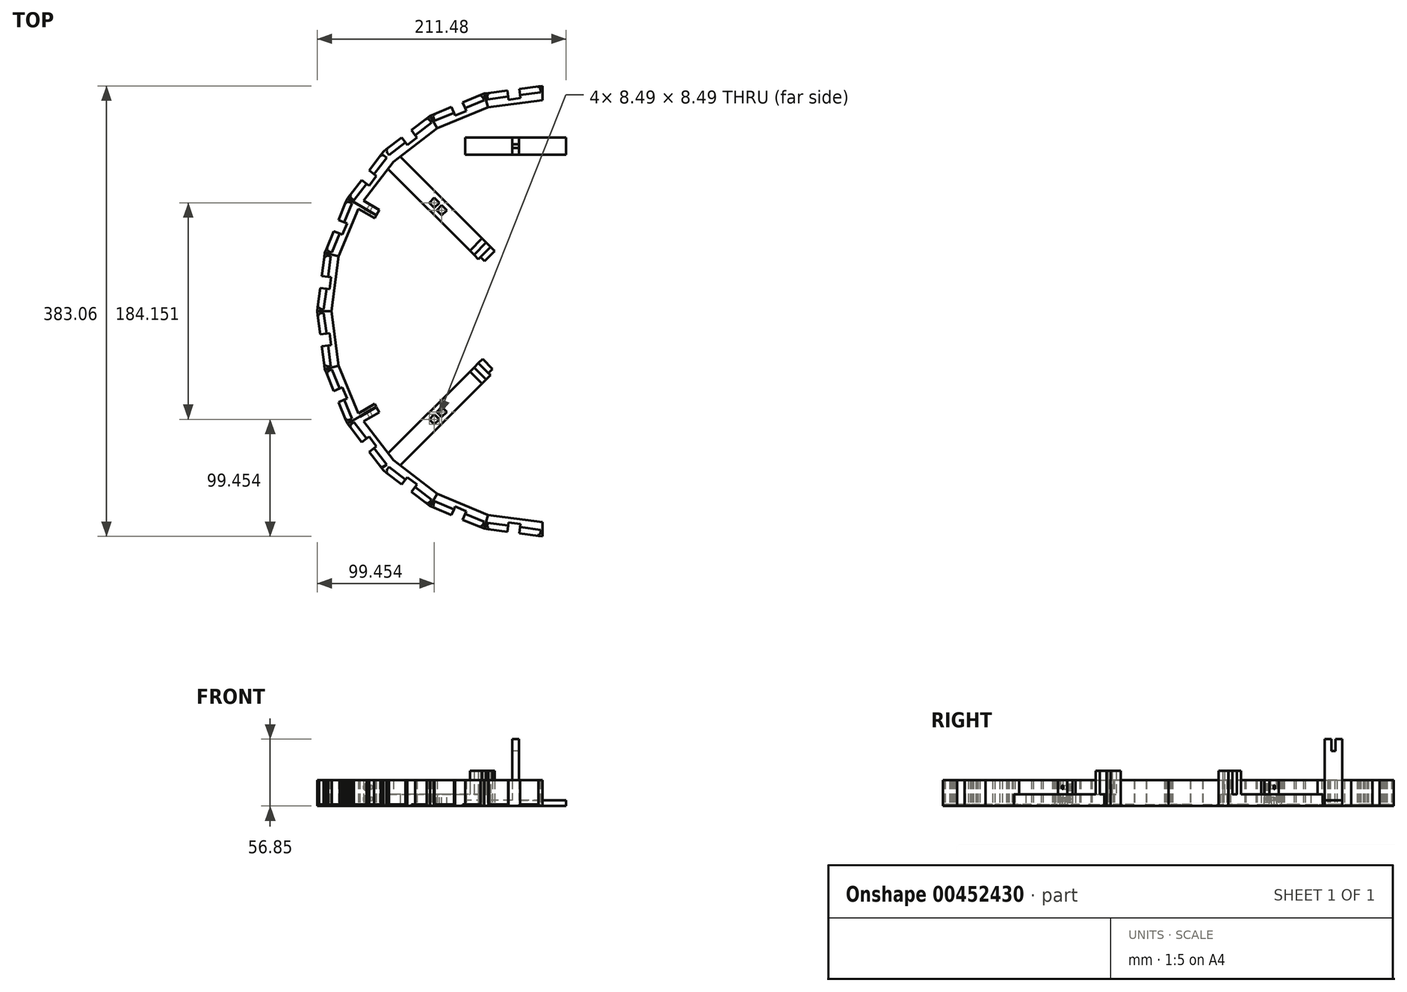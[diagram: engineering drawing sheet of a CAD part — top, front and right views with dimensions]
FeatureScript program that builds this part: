
annotation { "Feature Type Name" : "Feature", "Feature Type Description" : "" }
export const myFeature = defineFeature(function(context is Context, id is Id, definition is map)
    precondition{}
    {
        {
            var Q0;
            Q0=qCreatedBy(makeId("Top.planeOp"),FACE);
            var sketch = newSketch(context, id + "F0", { "sketchPlane" : qUnion([Q0])});
            skCircle(sketch, "E0.cCircle", {"center": v(0, 0) * mm, "radius": 75 * mm, "construction": true});
            skLineSegment(sketch, "E0.0", {"start": v(75, 31.07) * mm, "end": v(75, -31.07) * mm, "construction": true});
            skLineSegment(sketch, "E0.1", {"start": v(75, -31.07) * mm, "end": v(31.07, -75) * mm, "construction": true});
            skLineSegment(sketch, "E0.2", {"start": v(31.07, -75) * mm, "end": v(-31.07, -75) * mm, "construction": true});
            skLineSegment(sketch, "E0.3", {"start": v(-31.07, -75) * mm, "end": v(-75, -31.07) * mm, "construction": true});
            skLineSegment(sketch, "E0.4", {"start": v(-75, -31.07) * mm, "end": v(-75, 31.07) * mm, "construction": true});
            skLineSegment(sketch, "E0.5", {"start": v(-75, 31.07) * mm, "end": v(-31.07, 75) * mm, "construction": true});
            skLineSegment(sketch, "E0.6", {"start": v(-31.07, 75) * mm, "end": v(31.07, 75) * mm, "construction": true});
            skLineSegment(sketch, "E0.7", {"start": v(31.07, 75) * mm, "end": v(75, 31.07) * mm, "construction": true});
            skPoint(sketch, "E0.0.midPoint", {"position": v(74.36, -9.79) * mm});
            skPoint(sketch, "E1.endSnap0", {"position": v(0, -75) * mm});
            skArc(sketch, "E2.cCircle", {"start": v(0.47, 189.9) * mm, "mid": v(-189.9, 0.2) * mm, "end": v(0.07, -189.9) * mm, "construction": true});
            skLineSegment(sketch, "E2.1", {"start": v(0, -191.53) * mm, "end": v(-49.57, -185) * mm});
            skLineSegment(sketch, "E2.2", {"start": v(-49.57, -185) * mm, "end": v(-52.85, -183.65) * mm});
            skLineSegment(sketch, "E2.3", {"start": v(-95.77, -165.87) * mm, "end": v(-135.43, -135.43) * mm});
            skLineSegment(sketch, "E2.4", {"start": v(-135.43, -135.43) * mm, "end": v(-165.87, -95.77) * mm});
            skLineSegment(sketch, "E2.5", {"start": v(-165.87, -95.77) * mm, "end": v(-185, -49.57) * mm});
            skLineSegment(sketch, "E2.6", {"start": v(-185, -49.57) * mm, "end": v(-191.53, 0) * mm});
            skLineSegment(sketch, "E2.7", {"start": v(-191.53, 0) * mm, "end": v(-185, 49.57) * mm});
            skLineSegment(sketch, "E2.8", {"start": v(-185, 49.57) * mm, "end": v(-165.91, 95.67) * mm});
            skLineSegment(sketch, "E2.9", {"start": v(-165.81, 95.85) * mm, "end": v(-135.43, 135.43) * mm});
            skLineSegment(sketch, "E2.10", {"start": v(-135.43, 135.43) * mm, "end": v(-95.77, 165.87) * mm});
            skLineSegment(sketch, "E2.11", {"start": v(-95.77, 165.87) * mm, "end": v(-49.57, 185) * mm});
            skLineSegment(sketch, "E2.12", {"start": v(-49.57, 185) * mm, "end": v(0.47, 191.6) * mm});
            skLineSegment(sketch, "E3", {"start": v(0, 0) * mm, "end": v(-188.27, 24.79) * mm, "construction": true});
            skLineSegment(sketch, "E4.0", {"start": v(-46.44, 173.32) * mm, "end": v(0.46, 179.49) * mm});
            skLineSegment(sketch, "E4.1", {"start": v(-89.71, 155.39) * mm, "end": v(-46.44, 173.32) * mm});
            skLineSegment(sketch, "E4.2", {"start": v(-126.88, -126.88) * mm, "end": v(-155.39, -89.71) * mm});
            skLineSegment(sketch, "E4.3", {"start": v(-89.71, -155.39) * mm, "end": v(-126.88, -126.88) * mm});
            skLineSegment(sketch, "E4.4", {"start": v(-46.44, -173.32) * mm, "end": v(-89.71, -155.39) * mm});
            skLineSegment(sketch, "E4.5", {"start": v(0.5, -179.5) * mm, "end": v(-46.44, -173.32) * mm});
            skLineSegment(sketch, "E4.6", {"start": v(-155.39, -89.71) * mm, "end": v(-173.32, -46.44) * mm});
            skLineSegment(sketch, "E4.7", {"start": v(-173.32, -46.44) * mm, "end": v(-179.43, 0) * mm});
            skLineSegment(sketch, "E4.9", {"start": v(-173.32, 46.44) * mm, "end": v(-155.43, 89.62) * mm});
            skLineSegment(sketch, "E4.10", {"start": v(-155.33, 89.8) * mm, "end": v(-126.88, 126.88) * mm});
            skLineSegment(sketch, "E4.11", {"start": v(-126.88, 126.88) * mm, "end": v(-89.71, 155.39) * mm});
            skLineSegment(sketch, "E5", {"start": v(-72.67, -175.44) * mm, "end": v(-70.64, -170.54) * mm, "construction": true});
            skLineSegment(sketch, "E6", {"start": v(-65.88, -172.51) * mm, "end": v(-49.62, -179.25) * mm});
            skLineSegment(sketch, "E7", {"start": v(-75.4, -168.57) * mm, "end": v(-91.66, -161.84) * mm});
            skLineSegment(sketch, "E8", {"start": v(-49.62, -179.25) * mm, "end": v(-51.15, -182.94) * mm});
            skLineSegment(sketch, "E9", {"start": v(-91.66, -161.84) * mm, "end": v(-93.2, -165.53) * mm});
            skLineSegment(sketch, "E10", {"start": v(-93.2, -165.53) * mm, "end": v(-91.99, -166.03) * mm});
            skLineSegment(sketch, "E11", {"start": v(-91.99, -166.03) * mm, "end": v(-92.49, -167.23) * mm});
            skLineSegment(sketch, "E12", {"start": v(-51.15, -182.94) * mm, "end": v(-52.35, -182.45) * mm});
            skLineSegment(sketch, "E13", {"start": v(-52.35, -182.45) * mm, "end": v(-52.85, -183.65) * mm});
            skLineSegment(sketch, "E14.trimOffspring", {"start": v(-92.49, -167.23) * mm, "end": v(-95.77, -165.87) * mm});
            skLineSegment(sketch, "E15", {"start": v(-72.67, -175.44) * mm, "end": v(-69.65, -168.14) * mm, "construction": true});
            skLineSegment(sketch, "E16", {"start": v(-69.65, -168.14) * mm, "end": v(-64.89, -170.11) * mm});
            skLineSegment(sketch, "E17", {"start": v(-69.65, -168.14) * mm, "end": v(-74.4, -166.17) * mm});
            skLineSegment(sketch, "E18", {"start": v(-74.4, -166.17) * mm, "end": v(-75.4, -168.57) * mm});
            skLineSegment(sketch, "E19", {"start": v(-64.89, -170.11) * mm, "end": v(-65.88, -172.51) * mm});
            skLineSegment(sketch, "E20", {"start": v(-49.57, -185) * mm, "end": v(-46.44, -173.32) * mm});
            skLineSegment(sketch, "E21", {"start": v(-95.77, -165.87) * mm, "end": v(-89.71, -155.39) * mm});
            skLineSegment(sketch, "E22", {"start": v(-52.85, -183.65) * mm, "end": v(-92.49, -167.23) * mm});
            skLineSegment(sketch, "E23", {"start": v(-75.4, -168.57) * mm, "end": v(-77.43, -173.47) * mm});
            skLineSegment(sketch, "E24", {"start": v(-65.88, -172.51) * mm, "end": v(-67.91, -177.4) * mm, "construction": true});
            skLineSegment(sketch, "E25", {"start": v(-67.91, -177.4) * mm, "end": v(-65.88, -172.51) * mm});
            skLineSegment(sketch, "E26", {"start": v(-77.43, -173.47) * mm, "end": v(-75.4, -168.57) * mm, "construction": true});
            skLineSegment(sketch, "E27", {"start": v(-53.03, 53.03) * mm, "end": v(-126.88, 126.88) * mm, "construction": true});
            skLineSegment(sketch, "E28.0", {"start": v(-47.87, 58.2) * mm, "end": v(-121.03, 131.36) * mm});
            skLineSegment(sketch, "E29.0", {"start": v(-58.2, 47.87) * mm, "end": v(-131.36, 121.03) * mm});
            skLineSegment(sketch, "E30", {"start": v(-61.73, 51.4) * mm, "end": v(-51.4, 61.73) * mm});
            skLineSegment(sketch, "E31", {"start": v(-47.87, 58.2) * mm, "end": v(-44.2, 54.52) * mm});
            skLineSegment(sketch, "E32", {"start": v(-58.2, 47.87) * mm, "end": v(-54.52, 44.2) * mm});
            skLineSegment(sketch, "E33", {"start": v(-54.52, 44.2) * mm, "end": v(-44.2, 54.52) * mm});
            skLineSegment(sketch, "E34", {"start": v(-44.2, 54.52) * mm, "end": v(-40.66, 50.98) * mm});
            skLineSegment(sketch, "E35", {"start": v(-40.66, 50.98) * mm, "end": v(-49.14, 42.5) * mm});
            skLineSegment(sketch, "E36", {"start": v(-49.14, 42.5) * mm, "end": v(-52.68, 46.03) * mm});
            skLineSegment(sketch, "E37", {"start": v(-47.87, 58.2) * mm, "end": v(-58.2, 47.87) * mm});
            skLineSegment(sketch, "E38.1.0", {"start": v(-50.98, -40.66) * mm, "end": v(-42.5, -49.14) * mm});
            skLineSegment(sketch, "E38.1.1", {"start": v(-54.52, -44.2) * mm, "end": v(-50.98, -40.66) * mm});
            skLineSegment(sketch, "E38.1.2", {"start": v(-58.2, -47.87) * mm, "end": v(-54.52, -44.2) * mm});
            skLineSegment(sketch, "E38.1.3", {"start": v(-58.2, -47.87) * mm, "end": v(-47.87, -58.2) * mm});
            skLineSegment(sketch, "E38.1.4", {"start": v(-51.4, -61.73) * mm, "end": v(-61.73, -51.4) * mm});
            skLineSegment(sketch, "E38.1.5", {"start": v(-44.2, -54.52) * mm, "end": v(-54.52, -44.2) * mm});
            skLineSegment(sketch, "E38.1.6", {"start": v(-47.87, -58.2) * mm, "end": v(-44.2, -54.52) * mm});
            skLineSegment(sketch, "E38.1.7", {"start": v(-47.87, -58.2) * mm, "end": v(-121.03, -131.36) * mm});
            skLineSegment(sketch, "E38.1.8", {"start": v(-58.2, -47.87) * mm, "end": v(-131.36, -121.03) * mm});
            skLineSegment(sketch, "E38.anchor1", {"start": v(0, 0) * mm, "end": v(-49.14, 42.5) * mm, "construction": true});
            skLineSegment(sketch, "E38.anchor2", {"start": v(0, 0) * mm, "end": v(-42.5, -49.14) * mm, "construction": true});
            skLineSegment(sketch, "E39", {"start": v(-179.43, 0) * mm, "end": v(-191.53, 0) * mm});
            skLineSegment(sketch, "E40", {"start": v(0.07, -189.9) * mm, "end": v(0.47, 191.6) * mm, "construction": true});
            skPoint(sketch, "E41.orphan", {"position": v(0.5, 222.53) * mm});
            skLineSegment(sketch, "E42", {"start": v(-42.5, -49.14) * mm, "end": v(-46.03, -52.68) * mm});
            skLineSegment(sketch, "E43", {"start": v(-179.43, 0) * mm, "end": v(-173.32, 46.44) * mm});
            skLineSegment(sketch, "E44", {"start": v(-141.21, 81.64) * mm, "end": v(-138.71, 85.98) * mm});
            skLineSegment(sketch, "E45", {"start": v(-138.71, 85.98) * mm, "end": v(-152.26, 93.8) * mm});
            skLineSegment(sketch, "E46", {"start": v(-141.31, 81.47) * mm, "end": v(-142.76, 78.96) * mm});
            skLineSegment(sketch, "E47", {"start": v(-142.76, 78.96) * mm, "end": v(-156.55, 86.92) * mm});
            skLineSegment(sketch, "E48", {"start": v(0, 0) * mm, "end": v(-165.87, 95.77) * mm, "construction": true});
            skLineSegment(sketch, "E49", {"start": v(-141.21, 81.64) * mm, "end": v(-165.81, 95.85) * mm});
            skLineSegment(sketch, "E50", {"start": v(-165.91, 95.67) * mm, "end": v(-141.31, 81.47) * mm});
            skLineSegment(sketch, "E51", {"start": v(-155.43, 89.62) * mm, "end": v(-155.33, 89.8) * mm});
            skLineSegment(sketch, "E52", {"start": v(-165.91, 95.67) * mm, "end": v(-165.87, 95.77) * mm});
            skLineSegment(sketch, "E53", {"start": v(-165.87, 95.77) * mm, "end": v(-165.81, 95.85) * mm});
            skLineSegment(sketch, "E54.1.0", {"start": v(-141.31, -81.47) * mm, "end": v(-142.76, -78.96) * mm});
            skLineSegment(sketch, "E54.1.2", {"start": v(-141.31, -81.47) * mm, "end": v(-165.91, -95.67) * mm});
            skLineSegment(sketch, "E54.1.3", {"start": v(-165.81, -95.85) * mm, "end": v(-141.21, -81.64) * mm});
            skLineSegment(sketch, "E54.1.4", {"start": v(-155.33, -89.8) * mm, "end": v(-155.43, -89.62) * mm});
            skLineSegment(sketch, "E54.1.5", {"start": v(-138.71, -85.98) * mm, "end": v(-152.26, -93.8) * mm});
            skLineSegment(sketch, "E54.1.6", {"start": v(-141.21, -81.64) * mm, "end": v(-138.71, -85.98) * mm});
            skLineSegment(sketch, "E54.1.7", {"start": v(-165.81, -95.85) * mm, "end": v(-165.87, -95.77) * mm});
            skLineSegment(sketch, "E54.1.8", {"start": v(-165.87, -95.77) * mm, "end": v(-165.91, -95.67) * mm});
            skLineSegment(sketch, "E54.1.9", {"start": v(0, 0) * mm, "end": v(-165.87, -95.77) * mm, "construction": true});
            skLineSegment(sketch, "E54.anchor1", {"start": v(0, 0) * mm, "end": v(-165.91, 95.67) * mm, "construction": true});
            skLineSegment(sketch, "E54.anchor2", {"start": v(0, 0) * mm, "end": v(-165.81, -95.85) * mm, "construction": true});
            skLineSegment(sketch, "E55", {"start": v(-142.76, -78.96) * mm, "end": v(-156.55, -86.92) * mm});
            skSolve(sketch);
        }
        {
            var Q0;
            Q0=makeQuery(id+"F0.imprint","IMPRINT",FACE,{"disambiguationData":[TD([[makeQuery(id+"F0.imprint","IMPRINT",EDGE,{"derivedFrom":sQuery(id+"F0.wireOp",EDGE,"E2.2")}),-1.0]])]});
            extrude(context, id + "F1", {"entities" : qUnion([Q0]), "depth" : 22 * mm, "offsetDistance" : 25 * mm});
        }
        {
            var Q0;
            Q0=makeQuery(id+"F0.imprint","IMPRINT",FACE,{"disambiguationData":[TD([[makeQuery(id+"F0.imprint","IMPRINT",EDGE,{"derivedFrom":sQuery(id+"F0.wireOp",EDGE,"E6")}),-1.0]])]});
            var Q1;
            Q1=makeQuery(id+"F0.imprint","IMPRINT",FACE,{"disambiguationData":[TD([[makeQuery(id+"F0.imprint","IMPRINT",EDGE,{"derivedFrom":sQuery(id+"F0.wireOp",EDGE,"E7")}),1.0]])]});
            extrude(context, id + "F2", {"entities" : qUnion([Q0, Q1]), "operationType" : NewBodyOperationType.ADD, "depth" : 1.5 * mm, "offsetDistance" : 25 * mm});
        }
        {
            var Q0;
            Q0=qCreatedBy(makeId("Front.planeOp"),FACE);
            var sketch = newSketch(context, id + "F3", { "sketchPlane" : qUnion([Q0])});
            skLineSegment(sketch, "E56", {"start": v(0, 0) * mm, "end": v(0, 23.59) * mm, "construction": true});
            skSolve(sketch);
        }
        {
            var Q0;
            Q0=makeQuery(id+"F1.opExtrude","SWEPT_BODY",BODY,{"disambiguationData":[OSD([sQuery(id+"F0.wireOp",EDGE,"E2.2"),sQuery(id+"F0.wireOp",EDGE,"E4.4"),sQuery(id+"F0.wireOp",EDGE,"E6"),sQuery(id+"F0.wireOp",EDGE,"E7"),sQuery(id+"F0.wireOp",EDGE,"E8"),sQuery(id+"F0.wireOp",EDGE,"E9"),sQuery(id+"F0.wireOp",EDGE,"E10"),sQuery(id+"F0.wireOp",EDGE,"E11"),sQuery(id+"F0.wireOp",EDGE,"E12"),sQuery(id+"F0.wireOp",EDGE,"E13"),sQuery(id+"F0.wireOp",EDGE,"E14.trimOffspring"),sQuery(id+"F0.wireOp",EDGE,"E16"),sQuery(id+"F0.wireOp",EDGE,"E17"),sQuery(id+"F0.wireOp",EDGE,"E18"),sQuery(id+"F0.wireOp",EDGE,"E19"),sQuery(id+"F0.wireOp",EDGE,"E20"),sQuery(id+"F0.wireOp",EDGE,"E21")])]});
            var Q1;
            Q1=sQuery(id+"F3.wireOp",EDGE,"E56");
            transform(context, id + "F4", {"entities" : qUnion([Q0]), "transformType" : TransformType.ROTATION, "transformAxis" : qUnion([Q1]), "angle" : 15 * degree, "makeCopy" : true});
        }
        {
            var Q0;
            Q0=makeQuery(id+"F1.opExtrude","SWEPT_BODY",BODY,{"disambiguationData":[OSD([sQuery(id+"F0.wireOp",EDGE,"E2.2"),sQuery(id+"F0.wireOp",EDGE,"E4.4"),sQuery(id+"F0.wireOp",EDGE,"E6"),sQuery(id+"F0.wireOp",EDGE,"E7"),sQuery(id+"F0.wireOp",EDGE,"E8"),sQuery(id+"F0.wireOp",EDGE,"E9"),sQuery(id+"F0.wireOp",EDGE,"E10"),sQuery(id+"F0.wireOp",EDGE,"E11"),sQuery(id+"F0.wireOp",EDGE,"E12"),sQuery(id+"F0.wireOp",EDGE,"E13"),sQuery(id+"F0.wireOp",EDGE,"E14.trimOffspring"),sQuery(id+"F0.wireOp",EDGE,"E16"),sQuery(id+"F0.wireOp",EDGE,"E17"),sQuery(id+"F0.wireOp",EDGE,"E18"),sQuery(id+"F0.wireOp",EDGE,"E19"),sQuery(id+"F0.wireOp",EDGE,"E20"),sQuery(id+"F0.wireOp",EDGE,"E21")])]});
            var Q1;
            Q1=sQuery(id+"F3.wireOp",EDGE,"E56");
            circularPattern(context, id + "F5", {"entities" : qUnion([Q0]), "axis" : qUnion([Q1]), "angle" : 150 * degree, "instanceCount" : 11, "oppositeDirection" : true, "equalSpace" : true, "computeTransformsWithoutBuiltin" : true});
        }
        {
            var Q0;
            {var subQ3=sQuery(id+"F0.wireOp",EDGE,"E30");Q0=makeQuery(id+"F0.imprint","IMPRINT",FACE,{"disambiguationData":[TD([[makeQuery(id+"F0.imprint","IMPRINT",EDGE,{"derivedFrom":subQ3}),1.0]])]});}
            var Q1;
            {var subQ2=sQuery(id+"F0.wireOp",EDGE,"E30");Q1=makeQuery(id+"F0.imprint","IMPRINT",FACE,{"disambiguationData":[TD([[makeQuery(id+"F0.imprint","IMPRINT",EDGE,{"derivedFrom":subQ2}),-1.0]])]});}
            var Q2;
            {var subQ1=sQuery(id+"F0.wireOp",EDGE,"E31");Q2=makeQuery(id+"F0.imprint","IMPRINT",FACE,{"disambiguationData":[TD([[makeQuery(id+"F0.imprint","IMPRINT",EDGE,{"derivedFrom":subQ1}),-1.0]])]});}
            var Q3;
            {var subQ0=sQuery(id+"F0.wireOp",EDGE,"E34");Q3=makeQuery(id+"F0.imprint","IMPRINT",FACE,{"disambiguationData":[TD([[makeQuery(id+"F0.imprint","IMPRINT",EDGE,{"derivedFrom":subQ0}),-1.0]])]});}
            var Q4;
            {var subQ1=sQuery(id+"F0.wireOp",EDGE,"E38.1.4");Q4=makeQuery(id+"F0.imprint","IMPRINT",FACE,{"disambiguationData":[TD([[makeQuery(id+"F0.imprint","IMPRINT",EDGE,{"derivedFrom":subQ1}),1.0]])]});}
            var Q5;
            {var subQ0=sQuery(id+"F0.wireOp",EDGE,"E38.1.3");Q5=makeQuery(id+"F0.imprint","IMPRINT",FACE,{"disambiguationData":[TD([[makeQuery(id+"F0.imprint","IMPRINT",EDGE,{"derivedFrom":subQ0}),-1.0]])]});}
            var Q6;
            {var subQ1=sQuery(id+"F0.wireOp",EDGE,"E38.1.2");Q6=makeQuery(id+"F0.imprint","IMPRINT",FACE,{"disambiguationData":[TD([[makeQuery(id+"F0.imprint","IMPRINT",EDGE,{"derivedFrom":subQ1}),-1.0]])]});}
            var Q7;
            Q7=makeQuery(id+"F0.imprint","IMPRINT",FACE,{"disambiguationData":[TD([[makeQuery(id+"F0.imprint","IMPRINT",EDGE,{"derivedFrom":sQuery(id+"F0.wireOp",EDGE,"E38.1.0")}),-1.0]])]});
            extrude(context, id + "F6", {"entities" : qUnion([Q0, Q1, Q2, Q3, Q4, Q5, Q6, Q7]), "operationType" : NewBodyOperationType.ADD, "depth" : 5 * mm, "offsetDistance" : 25 * mm});
        }
        {
            var Q0;
            {var subQ2=sQuery(id+"F0.wireOp",EDGE,"E30");Q0=makeQuery(id+"F0.imprint","IMPRINT",FACE,{"disambiguationData":[TD([[makeQuery(id+"F0.imprint","IMPRINT",EDGE,{"derivedFrom":subQ2}),-1.0]])]});}
            var Q1;
            {var subQ0=sQuery(id+"F0.wireOp",EDGE,"E34");Q1=makeQuery(id+"F0.imprint","IMPRINT",FACE,{"disambiguationData":[TD([[makeQuery(id+"F0.imprint","IMPRINT",EDGE,{"derivedFrom":subQ0}),-1.0]])]});}
            var Q2;
            Q2=makeQuery(id+"F0.imprint","IMPRINT",FACE,{"disambiguationData":[TD([[makeQuery(id+"F0.imprint","IMPRINT",EDGE,{"derivedFrom":sQuery(id+"F0.wireOp",EDGE,"E38.1.0")}),-1.0]])]});
            var Q3;
            {var subQ0=sQuery(id+"F0.wireOp",EDGE,"E38.1.3");Q3=makeQuery(id+"F0.imprint","IMPRINT",FACE,{"disambiguationData":[TD([[makeQuery(id+"F0.imprint","IMPRINT",EDGE,{"derivedFrom":subQ0}),-1.0]])]});}
            extrude(context, id + "F7", {"entities" : qUnion([Q0, Q1, Q2, Q3]), "operationType" : NewBodyOperationType.ADD, "depth" : 30 * mm, "offsetDistance" : 25 * mm});
        }
        {
            var Q0;
            Q0=makeQuery(id+"F0.imprint","IMPRINT",FACE,{"disambiguationData":[TD([[makeQuery(id+"F0.imprint","IMPRINT",EDGE,{"derivedFrom":sQuery(id+"F0.wireOp",EDGE,"GCTjbCZ3-rWJ8-3Bt5-pqQ0-WsXmROxkx1kK")}),1.0]])]});
            var Q1;
            {var subQ0=sQuery(id+"F0.wireOp",EDGE,"EZpf3oR2-MSXJ-6veG-nYI6-mttKvzj23KY3");Q1=makeQuery(id+"F0.imprint","IMPRINT",FACE,{"disambiguationData":[TD([[makeQuery(id+"F0.imprint","IMPRINT",EDGE,{"derivedFrom":subQ0}),-1.0]])]});}
            var Q2;
            {var subQ3=sQuery(id+"F0.wireOp",EDGE,"E30");Q2=makeQuery(id+"F0.imprint","IMPRINT",FACE,{"disambiguationData":[TD([[makeQuery(id+"F0.imprint","IMPRINT",EDGE,{"derivedFrom":subQ3}),1.0]])]});}
            var Q3;
            {var subQ0=sQuery(id+"F0.wireOp",EDGE,"E34");Q3=makeQuery(id+"F0.imprint","IMPRINT",FACE,{"disambiguationData":[TD([[makeQuery(id+"F0.imprint","IMPRINT",EDGE,{"derivedFrom":subQ0}),-1.0]])]});}
            var Q4;
            Q4=makeQuery(id+"F0.imprint","IMPRINT",FACE,{"disambiguationData":[TD([[makeQuery(id+"F0.imprint","IMPRINT",EDGE,{"derivedFrom":sQuery(id+"F0.wireOp",EDGE,"E38.1.0")}),-1.0]])]});
            var Q5;
            {var subQ1=sQuery(id+"F0.wireOp",EDGE,"E38.1.4");Q5=makeQuery(id+"F0.imprint","IMPRINT",FACE,{"disambiguationData":[TD([[makeQuery(id+"F0.imprint","IMPRINT",EDGE,{"derivedFrom":subQ1}),1.0]])]});}
            var Q6;
            {var subQ2=sQuery(id+"F0.wireOp",EDGE,"E30");Q6=makeQuery(id+"F0.imprint","IMPRINT",FACE,{"disambiguationData":[TD([[makeQuery(id+"F0.imprint","IMPRINT",EDGE,{"derivedFrom":subQ2}),-1.0]])]});}
            var Q7;
            {var subQ1=sQuery(id+"F0.wireOp",EDGE,"E31");Q7=makeQuery(id+"F0.imprint","IMPRINT",FACE,{"disambiguationData":[TD([[makeQuery(id+"F0.imprint","IMPRINT",EDGE,{"derivedFrom":subQ1}),-1.0]])]});}
            var Q8;
            {var subQ1=sQuery(id+"F0.wireOp",EDGE,"E38.1.2");Q8=makeQuery(id+"F0.imprint","IMPRINT",FACE,{"disambiguationData":[TD([[makeQuery(id+"F0.imprint","IMPRINT",EDGE,{"derivedFrom":subQ1}),-1.0]])]});}
            var Q9;
            {var subQ0=sQuery(id+"F0.wireOp",EDGE,"E38.1.3");Q9=makeQuery(id+"F0.imprint","IMPRINT",FACE,{"disambiguationData":[TD([[makeQuery(id+"F0.imprint","IMPRINT",EDGE,{"derivedFrom":subQ0}),-1.0]])]});}
            extrude(context, id + "F8", {"entities" : qUnion([Q0, Q1, Q2, Q3, Q4, Q5, Q6, Q7, Q8, Q9]), "operationType" : NewBodyOperationType.ADD, "depth" : 10 * mm, "offsetDistance" : 25 * mm});
        }
        {
            var Q0;
            {var subQ0=sQuery(id+"F0.wireOp",EDGE,"E34");var subQ1=sQuery(id+"F0.wireOp",EDGE,"E31");var subQ2=sQuery(id+"F0.wireOp",EDGE,"E28.0");var subQ3=sQuery(id+"F0.wireOp",EDGE,"E32");var subQ4=sQuery(id+"F0.wireOp",EDGE,"E29.0");var subQ5=makeQuery(id+"F1.opExtrude","SWEPT_FACE",FACE,{"disambiguationData":[OSD([sQuery(id+"F0.wireOp",EDGE,"E4.4")])]});Q0=makeQuery(id+"F8.boolean.opBoolean","SPLIT",FACE,{"disambiguationData":[TD([makeQuery(id+"F5.opPattern","COPY",FACE,{"derivedFrom":subQ5,"instanceName":"7"})])],"derivedFrom":makeQuery(id+"F8.opExtrude","CAP_FACE",FACE,{"disambiguationData":[OSD([sQuery(id+"F0.wireOp",EDGE,"E4.10"),sQuery(id+"F0.wireOp",EDGE,"E4.11"),subQ2,subQ4,subQ1,subQ3,sQuery(id+"F0.wireOp",EDGE,"E33"),subQ0,sQuery(id+"F0.wireOp",EDGE,"E35"),sQuery(id+"F0.wireOp",EDGE,"E36")])],"isStart":false})});}
            var sketch = newSketch(context, id + "F9", { "sketchPlane" : qUnion([Q0])});
            skLineSegment(sketch, "E57.0", {"start": v(-53.03, 53.03) * mm, "end": v(-126.88, 126.88) * mm, "construction": true});
            skLineSegment(sketch, "E58", {"start": v(-89.95, 89.95) * mm, "end": v(-87.83, 92.08) * mm});
            skLineSegment(sketch, "E59", {"start": v(-89.95, 89.95) * mm, "end": v(-92.08, 87.83) * mm});
            skLineSegment(sketch, "E60", {"start": v(-87.83, 92.08) * mm, "end": v(-92.08, 96.32) * mm});
            skLineSegment(sketch, "E61", {"start": v(-92.08, 96.32) * mm, "end": v(-96.32, 92.08) * mm});
            skLineSegment(sketch, "E62", {"start": v(-96.32, 92.08) * mm, "end": v(-92.08, 87.83) * mm});
            skLineSegment(sketch, "E63", {"start": v(-87.83, 92.08) * mm, "end": v(-85.71, 89.95) * mm, "construction": true});
            skLineSegment(sketch, "E64", {"start": v(-85.71, 89.95) * mm, "end": v(-89.95, 85.71) * mm});
            skLineSegment(sketch, "E65", {"start": v(-89.95, 85.71) * mm, "end": v(-85.71, 81.47) * mm});
            skLineSegment(sketch, "E66", {"start": v(-85.71, 81.47) * mm, "end": v(-81.47, 85.71) * mm});
            skLineSegment(sketch, "E67", {"start": v(-81.47, 85.71) * mm, "end": v(-85.71, 89.95) * mm});
            skLineSegment(sketch, "E68.1.0", {"start": v(-89.95, -85.71) * mm, "end": v(-85.71, -89.95) * mm});
            skLineSegment(sketch, "E68.1.1", {"start": v(-85.71, -81.47) * mm, "end": v(-89.95, -85.71) * mm});
            skLineSegment(sketch, "E68.1.2", {"start": v(-81.47, -85.71) * mm, "end": v(-85.71, -81.47) * mm});
            skLineSegment(sketch, "E68.1.3", {"start": v(-85.71, -89.95) * mm, "end": v(-81.47, -85.71) * mm});
            skLineSegment(sketch, "E68.1.4", {"start": v(-53.03, -53.03) * mm, "end": v(-126.88, -126.88) * mm, "construction": true});
            skLineSegment(sketch, "E68.1.5", {"start": v(-89.95, -89.95) * mm, "end": v(-92.08, -87.83) * mm});
            skLineSegment(sketch, "E68.1.6", {"start": v(-92.08, -87.83) * mm, "end": v(-96.32, -92.08) * mm});
            skLineSegment(sketch, "E68.1.7", {"start": v(-96.32, -92.08) * mm, "end": v(-92.08, -96.32) * mm});
            skLineSegment(sketch, "E68.1.8", {"start": v(-92.08, -96.32) * mm, "end": v(-87.83, -92.08) * mm});
            skLineSegment(sketch, "E68.1.9", {"start": v(-89.95, -89.95) * mm, "end": v(-87.83, -92.08) * mm});
            skLineSegment(sketch, "E68.1.10", {"start": v(-92.08, -87.83) * mm, "end": v(-89.95, -85.71) * mm, "construction": true});
            skPoint(sketch, "E68.center", {"position": v(0, 0) * mm});
            skSolve(sketch);
        }
        {
            var Q0;
            Q0=makeQuery(id+"F9.imprint","IMPRINT",FACE,{"disambiguationData":[TD([[makeQuery(id+"F9.imprint","IMPRINT",EDGE,{"derivedFrom":sQuery(id+"F9.wireOp",EDGE,"E68.1.0")}),1.0]])]});
            var Q1;
            Q1=makeQuery(id+"F9.imprint","IMPRINT",FACE,{"disambiguationData":[TD([[makeQuery(id+"F9.imprint","IMPRINT",EDGE,{"derivedFrom":sQuery(id+"F9.wireOp",EDGE,"E68.1.5")}),1.0]])]});
            extrude(context, id + "F10", {"entities" : qUnion([Q0, Q1]), "operationType" : NewBodyOperationType.REMOVE, "oppositeDirection" : true, "depth" : 25 * mm, "offsetDistance" : 25 * mm});
        }
        {
            var Q0;
            Q0=makeQuery(id+"F9.imprint","IMPRINT",FACE,{"disambiguationData":[TD([[makeQuery(id+"F9.imprint","IMPRINT",EDGE,{"derivedFrom":sQuery(id+"F9.wireOp",EDGE,"E64")}),1.0]])]});
            var Q1;
            Q1=makeQuery(id+"F9.imprint","IMPRINT",FACE,{"disambiguationData":[TD([[makeQuery(id+"F9.imprint","IMPRINT",EDGE,{"derivedFrom":sQuery(id+"F9.wireOp",EDGE,"E58")}),1.0]])]});
            extrude(context, id + "F11", {"entities" : qUnion([Q0, Q1]), "operationType" : NewBodyOperationType.REMOVE, "oppositeDirection" : true, "depth" : 25 * mm, "offsetDistance" : 25 * mm});
        }
        {
            var Q0;
            Q0=qCreatedBy(makeId("Top.planeOp"),FACE);
            var sketch = newSketch(context, id + "F12", { "sketchPlane" : qUnion([Q0])});
            skLineSegment(sketch, "E69", {"start": v(-25.85, 147.69) * mm, "end": v(-20.05, 147.69) * mm});
            skLineSegment(sketch, "E70", {"start": v(-20.05, 147.69) * mm, "end": v(-20.05, 141.89) * mm});
            skLineSegment(sketch, "E71", {"start": v(-20.05, 141.89) * mm, "end": v(-25.85, 141.89) * mm});
            skLineSegment(sketch, "E72", {"start": v(-25.85, 141.89) * mm, "end": v(-25.85, 147.69) * mm});
            skLineSegment(sketch, "E73", {"start": v(-25.85, 141.89) * mm, "end": v(-25.85, 138.69) * mm, "construction": true});
            skLineSegment(sketch, "E74", {"start": v(-25.85, 138.69) * mm, "end": v(-20.05, 138.69) * mm});
            skLineSegment(sketch, "E75", {"start": v(-20.05, 138.69) * mm, "end": v(-20.05, 132.89) * mm});
            skLineSegment(sketch, "E76", {"start": v(-20.05, 132.89) * mm, "end": v(-25.85, 132.89) * mm});
            skLineSegment(sketch, "E77", {"start": v(-25.85, 132.89) * mm, "end": v(-25.85, 138.69) * mm});
            skLineSegment(sketch, "E78", {"start": v(-25.85, 147.69) * mm, "end": v(-65.85, 147.69) * mm});
            skLineSegment(sketch, "E79", {"start": v(-25.85, 132.89) * mm, "end": v(-65.85, 132.89) * mm});
            skLineSegment(sketch, "E80", {"start": v(-65.85, 132.89) * mm, "end": v(-65.85, 147.69) * mm});
            skLineSegment(sketch, "E81", {"start": v(-20.05, 147.69) * mm, "end": v(19.95, 147.69) * mm});
            skLineSegment(sketch, "E82", {"start": v(19.95, 147.69) * mm, "end": v(19.95, 132.89) * mm});
            skLineSegment(sketch, "E83", {"start": v(19.95, 132.89) * mm, "end": v(-20.05, 132.89) * mm});
            skLineSegment(sketch, "E84", {"start": v(-20.05, 138.69) * mm, "end": v(-20.05, 141.89) * mm});
            skLineSegment(sketch, "E85", {"start": v(-25.85, 138.69) * mm, "end": v(-25.85, 141.89) * mm});
            skSolve(sketch);
        }
        {
            var Q0;
            Q0=makeQuery(id+"F12.imprint","IMPRINT",FACE,{"disambiguationData":[TD([[makeQuery(id+"F12.imprint","IMPRINT",EDGE,{"derivedFrom":sQuery(id+"F12.wireOp",EDGE,"E71")}),1.0]])]});
            extrude(context, id + "F13", {"entities" : qUnion([Q0]), "depth" : 46.85 * mm, "offsetDistance" : 25 * mm});
        }
        {
            var Q0;
            Q0=makeQuery(id+"F12.imprint","IMPRINT",FACE,{"disambiguationData":[TD([[makeQuery(id+"F12.imprint","IMPRINT",EDGE,{"derivedFrom":sQuery(id+"F12.wireOp",EDGE,"E74")}),-1.0]])]});
            var Q1;
            Q1=makeQuery(id+"F12.imprint","IMPRINT",FACE,{"disambiguationData":[TD([[makeQuery(id+"F12.imprint","IMPRINT",EDGE,{"derivedFrom":sQuery(id+"F12.wireOp",EDGE,"E69")}),-1.0]])]});
            extrude(context, id + "F14", {"entities" : qUnion([Q0, Q1]), "operationType" : NewBodyOperationType.ADD, "depth" : 56.85 * mm, "offsetDistance" : 25 * mm});
        }
        {
            var Q0;
            Q0=makeQuery(id+"F12.imprint","IMPRINT",FACE,{"disambiguationData":[TD([[makeQuery(id+"F12.imprint","IMPRINT",EDGE,{"derivedFrom":sQuery(id+"F12.wireOp",EDGE,"E72")}),1.0]])]});
            var Q1;
            Q1=makeQuery(id+"F12.imprint","IMPRINT",FACE,{"disambiguationData":[TD([[makeQuery(id+"F12.imprint","IMPRINT",EDGE,{"derivedFrom":sQuery(id+"F12.wireOp",EDGE,"E70")}),1.0]])]});
            extrude(context, id + "F15", {"entities" : qUnion([Q0, Q1]), "operationType" : NewBodyOperationType.ADD, "depth" : 5 * mm, "offsetDistance" : 25 * mm});
        }
        {
            var Q0;
            {var subQ1=sQuery(id+"F0.wireOp",EDGE,"E51");Q0=makeQuery(id+"F0.imprint","IMPRINT",FACE,{"disambiguationData":[TD([[makeQuery(id+"F0.imprint","IMPRINT",EDGE,{"derivedFrom":subQ1}),1.0]])]});}
            var Q1;
            {var subQ0=sQuery(id+"F0.wireOp",EDGE,"E54.1.7");Q1=makeQuery(id+"F0.imprint","IMPRINT",FACE,{"disambiguationData":[TD([[makeQuery(id+"F0.imprint","IMPRINT",EDGE,{"derivedFrom":subQ0}),-1.0]])]});}
            extrude(context, id + "F16", {"entities" : qUnion([Q0, Q1]), "operationType" : NewBodyOperationType.REMOVE, "depth" : 26.5 * mm, "offsetDistance" : 25 * mm});
        }
        {
            var Q0;
            {var subQ4=sQuery(id+"F0.wireOp",EDGE,"E46");Q0=makeQuery(id+"F0.imprint","IMPRINT",FACE,{"disambiguationData":[TD([[makeQuery(id+"F0.imprint","IMPRINT",EDGE,{"derivedFrom":subQ4}),-1.0]])]});}
            extrude(context, id + "F17", {"entities" : qUnion([Q0]), "operationType" : NewBodyOperationType.ADD, "depth" : 22 * mm, "offsetDistance" : 25 * mm});
        }
        {
            var Q0;
            {var subQ4=sQuery(id+"F0.wireOp",EDGE,"E44");Q0=makeQuery(id+"F0.imprint","IMPRINT",FACE,{"disambiguationData":[TD([[makeQuery(id+"F0.imprint","IMPRINT",EDGE,{"derivedFrom":subQ4}),1.0]])]});}
            extrude(context, id + "F18", {"entities" : qUnion([Q0]), "operationType" : NewBodyOperationType.ADD, "depth" : 22 * mm, "offsetDistance" : 25 * mm});
        }
        {
            var Q0;
            {var subQ4=sQuery(id+"F0.wireOp",EDGE,"E54.1.0");Q0=makeQuery(id+"F0.imprint","IMPRINT",FACE,{"disambiguationData":[TD([[makeQuery(id+"F0.imprint","IMPRINT",EDGE,{"derivedFrom":subQ4}),1.0]])]});}
            extrude(context, id + "F19", {"entities" : qUnion([Q0]), "operationType" : NewBodyOperationType.ADD, "depth" : 22 * mm, "offsetDistance" : 25 * mm});
        }
        {
            var Q0;
            {var subQ3=sQuery(id+"F0.wireOp",EDGE,"E54.1.5");Q0=makeQuery(id+"F0.imprint","IMPRINT",FACE,{"disambiguationData":[TD([[makeQuery(id+"F0.imprint","IMPRINT",EDGE,{"derivedFrom":subQ3}),-1.0]])]});}
            extrude(context, id + "F20", {"entities" : qUnion([Q0]), "operationType" : NewBodyOperationType.ADD, "depth" : 22 * mm, "offsetDistance" : 25 * mm});
        }
        {
            var Q0;
            Q0=makeQuery(id+"F17.opExtrude","SWEPT_FACE",FACE,{"disambiguationData":[OSD([sQuery(id+"F0.wireOp",EDGE,"E47")])]});
            var sketch = newSketch(context, id + "F21", { "sketchPlane" : qUnion([Q0])});
            skPoint(sketch, "E86.0", {"position": v(-163.12, 22) * mm});
            skPoint(sketch, "E86.1", {"position": v(-163.12, 0) * mm});
            skLineSegment(sketch, "E87", {"start": v(-163.12, 22) * mm, "end": v(-163.12, 16) * mm, "construction": true});
            skLineSegment(sketch, "E88", {"start": v(-163.12, 16) * mm, "end": v(-171.12, 16) * mm, "construction": true});
            skLineSegment(sketch, "E89", {"start": v(-163.12, 0) * mm, "end": v(-163.12, 6) * mm, "construction": true});
            skLineSegment(sketch, "E90", {"start": v(-163.12, 6) * mm, "end": v(-171.12, 6) * mm, "construction": true});
            skCircle(sketch, "E91", {"center": v(-171.12, 16) * mm, "radius": 1 * mm});
            skCircle(sketch, "E92", {"center": v(-171.12, 16) * mm, "radius": 1.5 * mm});
            skCircle(sketch, "E93", {"center": v(-171.12, 16) * mm, "radius": 3 * mm});
            skCircle(sketch, "E94", {"center": v(-171.12, 6) * mm, "radius": 1 * mm});
            skCircle(sketch, "E95", {"center": v(-171.12, 6) * mm, "radius": 1.5 * mm});
            skCircle(sketch, "E96", {"center": v(-171.12, 6) * mm, "radius": 3 * mm});
            skSolve(sketch);
        }
        {
            var Q0;
            Q0=makeQuery(id+"F21.imprint","IMPRINT",FACE,{"disambiguationData":[TD([[makeQuery(id+"F21.imprint","IMPRINT",EDGE,{"derivedFrom":sQuery(id+"F21.wireOp",EDGE,"E91")}),1.0]])]});
            var Q1;
            Q1=makeQuery(id+"F21.imprint","IMPRINT",FACE,{"disambiguationData":[TD([[makeQuery(id+"F21.imprint","IMPRINT",EDGE,{"derivedFrom":sQuery(id+"F21.wireOp",EDGE,"E94")}),1.0]])]});
            extrude(context, id + "F22", {"entities" : qUnion([Q0, Q1]), "operationType" : NewBodyOperationType.REMOVE, "oppositeDirection" : true, "depth" : 10.4 * mm, "offsetDistance" : 25 * mm});
        }
        {
            var Q0;
            Q0=makeQuery(id+"F21.imprint","IMPRINT",FACE,{"disambiguationData":[TD([[makeQuery(id+"F21.imprint","IMPRINT",EDGE,{"derivedFrom":sQuery(id+"F21.wireOp",EDGE,"E91")}),-1.0]])]});
            var Q1;
            Q1=makeQuery(id+"F21.imprint","IMPRINT",FACE,{"disambiguationData":[TD([[makeQuery(id+"F21.imprint","IMPRINT",EDGE,{"derivedFrom":sQuery(id+"F21.wireOp",EDGE,"E94")}),-1.0]])]});
            extrude(context, id + "F23", {"entities" : qUnion([Q0, Q1]), "operationType" : NewBodyOperationType.REMOVE, "oppositeDirection" : true, "depth" : 25 * mm, "offsetDistance" : 25 * mm});
        }
        {
            var Q0;
            Q0=makeQuery(id+"F21.imprint","IMPRINT",FACE,{"disambiguationData":[TD([[makeQuery(id+"F21.imprint","IMPRINT",EDGE,{"derivedFrom":sQuery(id+"F21.wireOp",EDGE,"E92")}),-1.0]])]});
            var Q1;
            Q1=makeQuery(id+"F21.imprint","IMPRINT",FACE,{"disambiguationData":[TD([[makeQuery(id+"F21.imprint","IMPRINT",EDGE,{"derivedFrom":sQuery(id+"F21.wireOp",EDGE,"E95")}),-1.0]])]});
            extrude(context, id + "F24", {"entities" : qUnion([Q0, Q1]), "operationType" : NewBodyOperationType.REMOVE, "oppositeDirection" : true, "depth" : 2 * mm, "offsetDistance" : 25 * mm});
        }
        {
            var Q0;
            Q0=makeQuery(id+"F19.opExtrude","SWEPT_FACE",FACE,{"disambiguationData":[OSD([sQuery(id+"F0.wireOp",EDGE,"E55")])]});
            var sketch = newSketch(context, id + "F25", { "sketchPlane" : qUnion([Q0])});
            skPoint(sketch, "E97.0", {"position": v(163.12, 22) * mm});
            skPoint(sketch, "E97.1", {"position": v(163.12, 0) * mm});
            skLineSegment(sketch, "E98", {"start": v(163.12, 22) * mm, "end": v(163.12, 16) * mm, "construction": true});
            skLineSegment(sketch, "E99", {"start": v(163.12, 16) * mm, "end": v(171.12, 16) * mm, "construction": true});
            skLineSegment(sketch, "E100", {"start": v(163.12, 0) * mm, "end": v(163.12, 6) * mm, "construction": true});
            skLineSegment(sketch, "E101", {"start": v(163.12, 6) * mm, "end": v(171.12, 6) * mm, "construction": true});
            skCircle(sketch, "E102", {"center": v(171.12, 16) * mm, "radius": 1 * mm});
            skCircle(sketch, "E103", {"center": v(171.12, 16) * mm, "radius": 1.5 * mm});
            skCircle(sketch, "E104", {"center": v(171.12, 16) * mm, "radius": 3 * mm});
            skCircle(sketch, "E105", {"center": v(171.12, 6) * mm, "radius": 1 * mm});
            skCircle(sketch, "E106", {"center": v(171.12, 6) * mm, "radius": 1.5 * mm});
            skCircle(sketch, "E107", {"center": v(171.12, 6) * mm, "radius": 3 * mm});
            skSolve(sketch);
        }
        {
            var Q0;
            Q0=makeQuery(id+"F25.imprint","IMPRINT",FACE,{"disambiguationData":[TD([[makeQuery(id+"F25.imprint","IMPRINT",EDGE,{"derivedFrom":sQuery(id+"F25.wireOp",EDGE,"E102")}),1.0]])]});
            var Q1;
            Q1=makeQuery(id+"F25.imprint","IMPRINT",FACE,{"disambiguationData":[TD([[makeQuery(id+"F25.imprint","IMPRINT",EDGE,{"derivedFrom":sQuery(id+"F25.wireOp",EDGE,"E105")}),1.0]])]});
            extrude(context, id + "F26", {"entities" : qUnion([Q0, Q1]), "operationType" : NewBodyOperationType.REMOVE, "oppositeDirection" : true, "depth" : 10.3 * mm, "offsetDistance" : 25 * mm});
        }
        {
            var Q0;
            Q0=makeQuery(id+"F25.imprint","IMPRINT",FACE,{"disambiguationData":[TD([[makeQuery(id+"F25.imprint","IMPRINT",EDGE,{"derivedFrom":sQuery(id+"F25.wireOp",EDGE,"E102")}),-1.0]])]});
            var Q1;
            Q1=makeQuery(id+"F25.imprint","IMPRINT",FACE,{"disambiguationData":[TD([[makeQuery(id+"F25.imprint","IMPRINT",EDGE,{"derivedFrom":sQuery(id+"F25.wireOp",EDGE,"E105")}),-1.0]])]});
            extrude(context, id + "F27", {"entities" : qUnion([Q0, Q1]), "operationType" : NewBodyOperationType.REMOVE, "oppositeDirection" : true, "depth" : 8.2 * mm, "offsetDistance" : 25 * mm});
        }
        {
            var Q0;
            Q0=makeQuery(id+"F25.imprint","IMPRINT",FACE,{"disambiguationData":[TD([[makeQuery(id+"F25.imprint","IMPRINT",EDGE,{"derivedFrom":sQuery(id+"F25.wireOp",EDGE,"E103")}),-1.0]])]});
            var Q1;
            Q1=makeQuery(id+"F25.imprint","IMPRINT",FACE,{"disambiguationData":[TD([[makeQuery(id+"F25.imprint","IMPRINT",EDGE,{"derivedFrom":sQuery(id+"F25.wireOp",EDGE,"E106")}),-1.0]])]});
            extrude(context, id + "F28", {"entities" : qUnion([Q0, Q1]), "operationType" : NewBodyOperationType.REMOVE, "oppositeDirection" : true, "depth" : 2 * mm, "offsetDistance" : 25 * mm});
        }
    });
